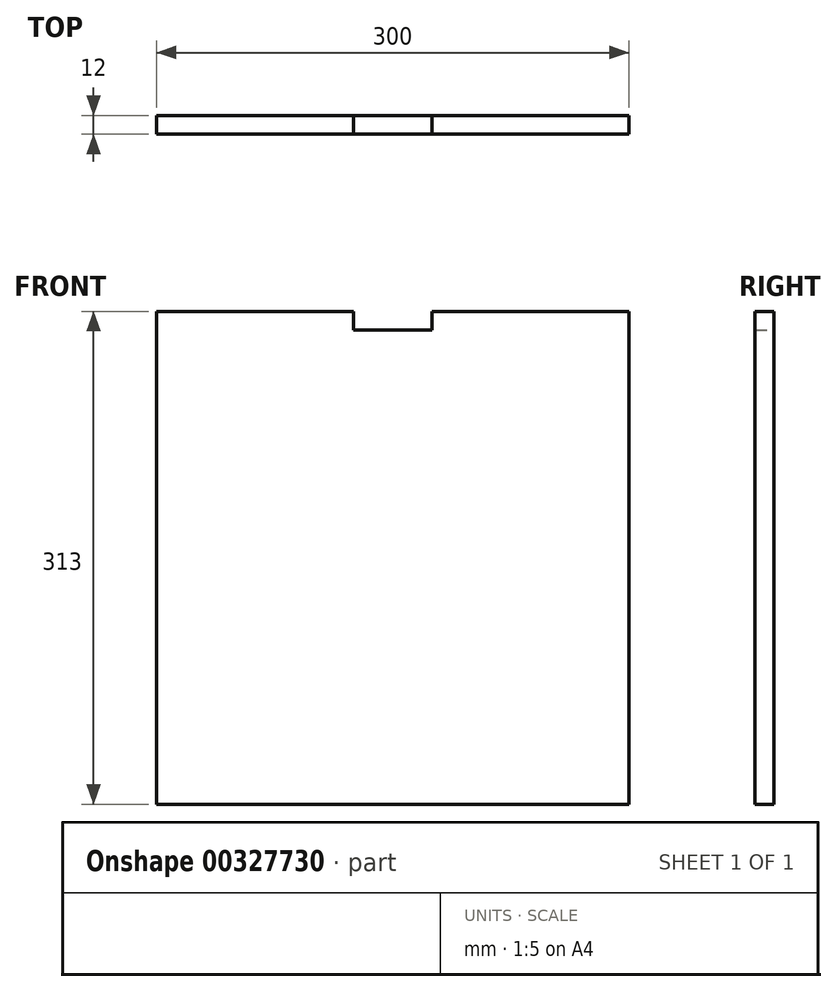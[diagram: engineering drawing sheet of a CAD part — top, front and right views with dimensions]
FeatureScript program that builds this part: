
annotation { "Feature Type Name" : "Feature", "Feature Type Description" : "" }
export const myFeature = defineFeature(function(context is Context, id is Id, definition is map)
    precondition{}
    {
        {
            var Q0;
            Q0=qCreatedBy(makeId("Front.planeOp"),FACE);
            var sketch = newSketch(context, id + "F0", { "sketchPlane" : qUnion([Q0])});
            skLineSegment(sketch, "E0", {"start": v(-46.12, 181.72) * mm, "end": v(-46.12, 169.72) * mm});
            skLineSegment(sketch, "E1", {"start": v(3.88, 169.72) * mm, "end": v(3.88, 181.72) * mm});
            skLineSegment(sketch, "E2.MirrorCS", {"start": v(-46.12, 181.72) * mm, "end": v(-171.12, 181.72) * mm});
            skLineSegment(sketch, "E3.MirrorCS", {"start": v(3.88, 181.72) * mm, "end": v(128.88, 181.72) * mm});
            skLineSegment(sketch, "E4", {"start": v(-46.12, 169.72) * mm, "end": v(3.88, 169.72) * mm});
            skLineSegment(sketch, "E5", {"start": v(-171.12, -131.28) * mm, "end": v(128.88, -131.28) * mm});
            skLineSegment(sketch, "E6", {"start": v(-171.12, 181.72) * mm, "end": v(-171.12, -131.28) * mm});
            skLineSegment(sketch, "E7", {"start": v(128.88, 181.72) * mm, "end": v(128.88, -131.28) * mm});
            skSolve(sketch);
        }
        {
            var Q0;
            Q0 = qSketchRegion(id + "F0", true);
            extrude(context, id + "F1", {"entities" : qUnion([Q0]), "depth" : 12 * mm});
        }
    });
